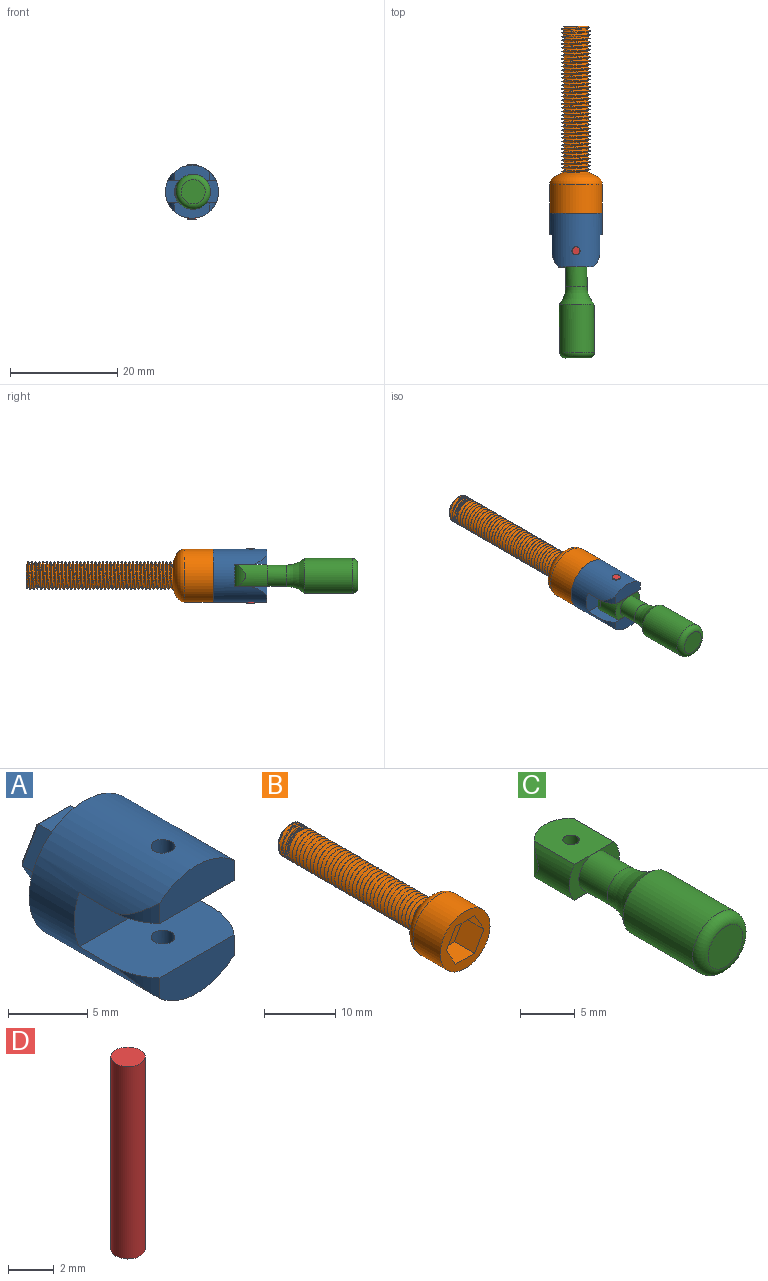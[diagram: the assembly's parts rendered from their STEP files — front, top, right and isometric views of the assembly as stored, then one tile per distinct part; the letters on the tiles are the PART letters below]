
ASSEMBLY  parts=4 mates=3
PART A: 26 faces, bbox 9.9x13x9.9 mm
  f0: plane 9.89x9.89mm, normal (0,1,0), area 55.2mm2, adj f3,f13,f14,f15,f16,f17,f18
  f1: plane 6.65x2.85mm, normal (0,-1,0), area 16.2mm2, adj f3,f4,f11,f12
  f2: plane 6.65x2.85mm, normal (0,-1,0), area 16.2mm2, adj f3,f5,f9,f10
  f3: cylinder r=4.94mm len=10mm, axis (0,1,0), area 246.9mm2, adj f0,f1,f2,f4,f5,f6,f7,f8
  f4: plane 8.95x6mm, normal (0,0,-1), area 49.8mm2, adj f1,f3,f6,f8,f11,f12
  f5: plane 8.95x6mm, normal (0,0,1), area 49.8mm2, adj f2,f3,f6,f7,f9,f10
  f6: plane 9.89x4.2mm, normal (0,-1,0), area 40.3mm2, adj f3,f4,f5
  f7: cylinder r=0.75mm len=2.85mm, axis (0,0,1), area 13.3mm2, adj f3,f5
  f8: cylinder r=0.75mm len=2.85mm, axis (0,0,1), area 13.3mm2, adj f3,f4
  f9: cylinder r=4.48mm len=3mm, axis (0,0,1), area 2mm2, adj f2,f3,f5
  f10: cylinder r=4.48mm len=3mm, axis (0,0,1), area 2mm2, adj f2,f3,f5
  f11: cylinder r=4.48mm len=3mm, axis (0,0,1), area 2mm2, adj f1,f3,f4
  f12: cylinder r=4.48mm len=3mm, axis (0,0,1), area 2mm2, adj f1,f3,f4
  f13: plane 2.7x2.5mm, normal (0.87,0,-0.5), area 7.8mm2, adj f0,f14,f18,f25
  f14: plane 2.89x2.7mm, normal (0,0,-1), area 7.8mm2, adj f0,f13,f15,f24
  f15: plane 2.7x2.5mm, normal (-0.87,0,-0.5), area 7.8mm2, adj f0,f14,f16,f22
  f16: plane 2.7x2.5mm, normal (-0.87,0,0.5), area 7.8mm2, adj f0,f15,f17,f20
  f17: plane 2.89x2.7mm, normal (0,0,1), area 7.8mm2, adj f0,f16,f18,f21
  f18: plane 2.7x2.5mm, normal (0.87,0,0.5), area 7.8mm2, adj f0,f13,f17,f23
  f19: plane 5.08x4.4mm, normal (0,1,0), area 16.8mm2, adj f20,f21,f22,f23,f24,f25
  f20: plane 2.5x1.62mm, normal (-0.61,0.71,0.35), area 1.2mm2, adj f16,f19,f21,f22
  f21: plane 2.89x0.3mm, normal (0,0.71,0.71), area 1.2mm2, adj f17,f19,f20,f23
  f22: plane 2.5x1.62mm, normal (-0.61,0.71,-0.35), area 1.2mm2, adj f15,f19,f20,f24
  f23: plane 2.5x1.62mm, normal (0.61,0.71,0.35), area 1.2mm2, adj f18,f19,f21,f25
  f24: plane 2.89x0.3mm, normal (0,0.71,-0.71), area 1.2mm2, adj f14,f19,f22,f25
  f25: plane 2.5x1.62mm, normal (0.61,0.71,-0.35), area 1.2mm2, adj f13,f19,f23,f24
PART B: 57 faces, bbox 9.9x35.3x9.9 mm
  f0: plane 4.32x4.32mm, normal (0,1,0), area 14.5mm2, adj f12
  f1: cylinder r=2.65mm len=27.19mm, axis (0,1,0), area -84.1mm2, adj f4,f52,f53,f55,f56
  f2: plane 9.89x9.89mm, normal (0,-1,0), area 40.6mm2, adj f3,f5,f6,f7,f8,f9,f10
  f3: cylinder r=4.94mm len=9.89mm, axis (0,1,0), area 168.1mm2, adj f2,f4
  f4: revolved ~9.89x9.89mm, area 84mm2, adj f1,f3,f54
  f5: plane 4x3.23mm, normal (0.87,0,0.5), area 14.9mm2, adj f2,f6,f10,f11
  f6: plane 4x3.73mm, normal (0,0,1), area 14.9mm2, adj f2,f5,f7,f11
  f7: plane 4x3.23mm, normal (-0.87,0,0.5), area 14.9mm2, adj f2,f6,f8,f11
  f8: plane 4x3.23mm, normal (-0.87,0,-0.5), area 14.9mm2, adj f2,f7,f9,f11
  f9: plane 4x3.73mm, normal (0,0,-1), area 14.9mm2, adj f2,f8,f10,f11
  f10: plane 4x3.23mm, normal (0.87,0,-0.5), area 14.9mm2, adj f2,f5,f9,f11
  f11: plane 7.46x6.46mm, normal (0,-1,0), area 36.2mm2, adj f5,f6,f7,f8,f9,f10
  f12: cylinder r=2.15mm len=4.29mm, axis (0,1,0), area 1.7mm2, adj f0,f51,f52,f55,f56
  f13: cylinder r=2.15mm len=2.99mm, axis (0,1,0), area 0.4mm2, adj f14,f52,f53,f55
  f14: cylinder r=2.15mm len=4.29mm, axis (0,1,0), area 1.2mm2, adj f13,f15,f52,f55
  f15: cylinder r=2.15mm len=4.29mm, axis (0,1,0), area 1.2mm2, adj f14,f16,f52,f55
  f16: cylinder r=2.15mm len=4.29mm, axis (0,1,0), area 1.1mm2, adj f15,f17,f52,f55
  f17: cylinder r=2.15mm len=4.29mm, axis (0,1,0), area 1.2mm2, adj f16,f18,f52,f55
  f18: cylinder r=2.15mm len=4.29mm, axis (0,1,0), area 1.1mm2, adj f17,f19,f52,f55
  f19: cylinder r=2.15mm len=4.29mm, axis (0,1,0), area 1.2mm2, adj f18,f20,f52,f55
  f20: cylinder r=2.15mm len=4.29mm, axis (0,1,0), area 1.1mm2, adj f19,f21,f52,f55
  f21: cylinder r=2.15mm len=4.29mm, axis (0,1,0), area 1.2mm2, adj f20,f22,f52,f55
  f22: cylinder r=2.15mm len=4.29mm, axis (0,1,0), area 1.1mm2, adj f21,f23,f52,f55
  f23: cylinder r=2.15mm len=4.29mm, axis (0,1,0), area 1.2mm2, adj f22,f24,f52,f55
  f24: cylinder r=2.15mm len=4.29mm, axis (0,1,0), area 1.1mm2, adj f23,f25,f52,f55
  f25: cylinder r=2.15mm len=4.29mm, axis (0,1,0), area 1.2mm2, adj f24,f26,f52,f55
  f26: cylinder r=2.15mm len=4.29mm, axis (0,1,0), area 1.1mm2, adj f25,f27,f52,f55
  f27: cylinder r=2.15mm len=4.29mm, axis (0,1,0), area 1.2mm2, adj f26,f28,f52,f55
  f28: cylinder r=2.15mm len=4.29mm, axis (0,1,0), area 1.2mm2, adj f27,f29,f52,f55
  f29: cylinder r=2.15mm len=4.29mm, axis (0,1,0), area 1.2mm2, adj f28,f30,f52,f55
  f30: cylinder r=2.15mm len=4.29mm, axis (0,1,0), area 1.2mm2, adj f29,f31,f52,f55
  f31: cylinder r=2.15mm len=4.29mm, axis (0,1,0), area 1.2mm2, adj f30,f32,f52,f55
  f32: cylinder r=2.15mm len=4.29mm, axis (0,1,0), area 1.2mm2, adj f31,f33,f52,f55
  f33: cylinder r=2.15mm len=4.29mm, axis (0,1,0), area 1.2mm2, adj f32,f34,f52,f55
  f34: cylinder r=2.15mm len=4.29mm, axis (0,1,0), area 1.2mm2, adj f33,f35,f52,f55
  f35: cylinder r=2.15mm len=4.29mm, axis (0,1,0), area 1.1mm2, adj f34,f36,f52,f55
  f36: cylinder r=2.15mm len=4.29mm, axis (0,1,0), area 1.2mm2, adj f35,f37,f52,f55
  f37: cylinder r=2.15mm len=4.29mm, axis (0,1,0), area 1.1mm2, adj f36,f38,f52,f55
  f38: cylinder r=2.15mm len=4.29mm, axis (0,1,0), area 1.2mm2, adj f37,f39,f52,f55
  f39: cylinder r=2.15mm len=4.29mm, axis (0,1,0), area 1.1mm2, adj f38,f40,f52,f55
  f40: cylinder r=2.15mm len=4.29mm, axis (0,1,0), area 1.2mm2, adj f39,f41,f52,f55
  f41: cylinder r=2.15mm len=4.29mm, axis (0,1,0), area 1.1mm2, adj f40,f42,f52,f55
  f42: cylinder r=2.15mm len=4.29mm, axis (0,1,0), area 1.2mm2, adj f41,f43,f52,f55
  f43: cylinder r=2.15mm len=4.29mm, axis (0,1,0), area 1.1mm2, adj f42,f44,f52,f55
  f44: cylinder r=2.15mm len=4.29mm, axis (0,1,0), area 1.2mm2, adj f43,f45,f52,f55
  f45: cylinder r=2.15mm len=4.29mm, axis (0,1,0), area 1.2mm2, adj f44,f46,f52,f55
  f46: cylinder r=2.15mm len=4.29mm, axis (0,1,0), area 1.2mm2, adj f45,f47,f52,f55
  f47: cylinder r=2.15mm len=4.29mm, axis (0,1,0), area 1.2mm2, adj f46,f48,f52,f55
  f48: cylinder r=2.15mm len=4.29mm, axis (0,1,0), area 1.2mm2, adj f47,f49,f52,f55
  f49: cylinder r=2.15mm len=4.29mm, axis (0,1,0), area 1.2mm2, adj f48,f50,f52,f55
  f50: cylinder r=2.15mm len=4.29mm, axis (0,1,0), area 1.2mm2, adj f49,f51,f52,f55
  f51: cylinder r=2.15mm len=4.29mm, axis (0,1,0), area 1.2mm2, adj f12,f50,f52,f55
  f52: bspline ~27.82x6.11mm, area 334.7mm2, adj f1,f12,f13,f14,f15,f16,f17,f18
  f53: plane 0.66x0.5mm, normal (0,0,1), area 0.2mm2, adj f1,f13,f52,f54,f55
  f54: cylinder r=2.65mm len=5.24mm, axis (0,1,0), area 1.3mm2, adj f4,f53,f55
  f55: bspline ~27.82x6.11mm, area 340.4mm2, adj f1,f12,f13,f14,f15,f16,f17,f18
  f56: cone r=2.64mm half-angle=60deg, axis (0,-1,0), area 3.9mm2, adj f1,f12,f52,f55
PART C: 13 faces, bbox 7.5x23.4x7.5 mm
  f0: plane 6.4x5.12mm, normal (0,0,1), area 29.2mm2, adj f2,f3,f7,f8,f9,f12
  f1: plane 6.4x5.12mm, normal (0,0,-1), area 29.2mm2, adj f2,f3,f7,f8,f9,f12
  f2: cylinder r=3.25mm len=5.24mm, axis (0,1,0), area 19.4mm2, adj f0,f1,f7,f12
  f3: cylinder r=3.25mm len=5.24mm, axis (0,1,0), area 19.4mm2, adj f0,f1,f8,f12
  f4: cylinder r=2mm len=4mm, axis (0,-1,0), area 46.4mm2, adj f7,f8,f10
  f5: cylinder r=3.25mm len=9mm, axis (0,1,0), area 183.8mm2, adj f10,f11
  f6: plane 4.5x4.5mm, normal (0,-1,0), area 15.9mm2, adj f11
  f7: plane 4x3.25mm, normal (0,-1,0), area 5.8mm2, adj f0,f1,f2,f4
  f8: plane 4x3.25mm, normal (0,-1,0), area 5.8mm2, adj f0,f1,f3,f4
  f9: cylinder r=0.75mm len=4mm, axis (0,0,1), area 18.8mm2, adj f0,f1
  f10: torus R=7mm, axis (0,-1,0), area 55mm2, adj f4,f5
  f11: torus R=2.25mm, axis (0,-1,0), area 28.5mm2, adj f5,f6
  f12: cylinder r=3.4mm len=6.5mm, axis (0,0,-1), area 30.4mm2, adj f0,f1,f2,f3
PART D: 3 faces, bbox 1.5x1.5x10.3 mm
  f0: cylinder r=0.75mm len=10.32mm, axis (0,0,-1), area 48.6mm2, adj f1,f2
  f1: plane 1.5x1.5mm, normal (0,0,1), area 1.8mm2, adj f0
  f2: plane 1.5x1.5mm, normal (0,0,-1), area 1.8mm2, adj f0
PLACE A t=(0.37,1.98,-1.88)mm fixed
PLACE B t=(0.37,1.98,-1.88)mm
PLACE C rot(axis=(0,0,1),0.7deg) t=(0.29,1.98,-1.9)mm
PLACE D t=(0.37,1.98,-1.97)mm
MATE fastened A.f3 <-> B.f1  axis (0,1,0) through (0.37,1.98,-1.88)mm
MATE revolute C.f9 <-> D.f0  axis (0,0,-1) through (0.37,-5.02,-3.9)mm
MATE fastened A.f7 <-> D.f0  axis (0,0,-1) through (0.37,-5.02,0.22)mm
